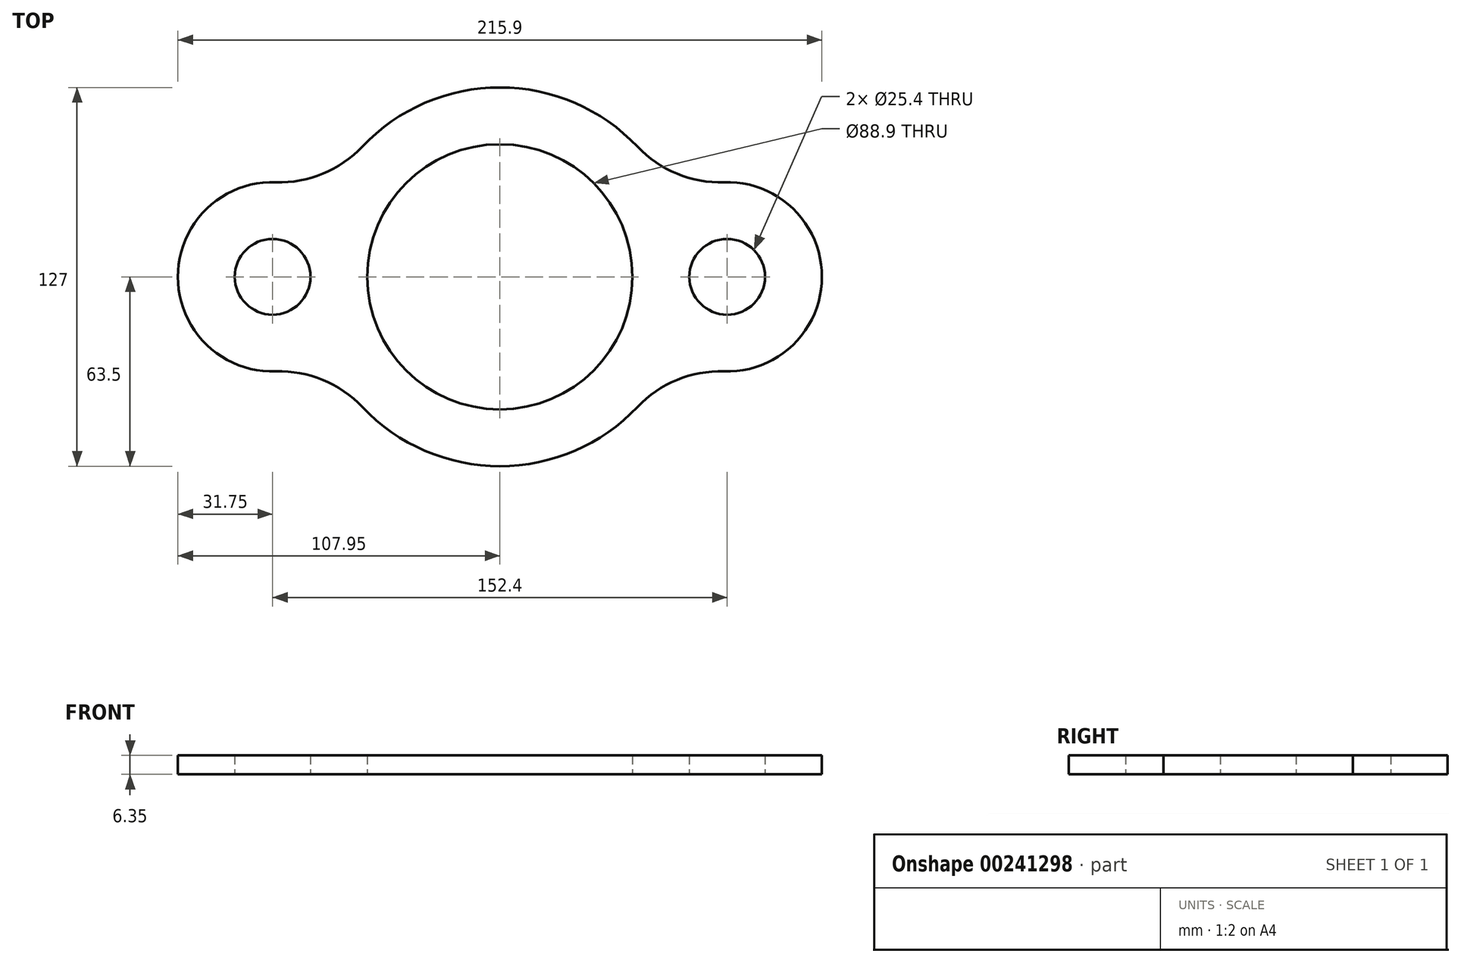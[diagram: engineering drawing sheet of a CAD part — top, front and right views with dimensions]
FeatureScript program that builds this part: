
annotation { "Feature Type Name" : "Feature", "Feature Type Description" : "" }
export const myFeature = defineFeature(function(context is Context, id is Id, definition is map)
    precondition{}
    {
        {
            var Q0;
            Q0=qCreatedBy(makeId("Top.planeOp"),FACE);
            var sketch = newSketch(context, id + "F0", { "sketchPlane" : qUnion([Q0])});
            skCircle(sketch, "E0", {"center": v(0, 0) * mm, "radius": 44.45 * mm});
            skArc(sketch, "E1", {"start": v(-46.14, -43.63) * mm, "mid": v(0, -63.5) * mm, "end": v(46.14, -43.63) * mm});
            skCircle(sketch, "E2", {"center": v(-76.2, 0) * mm, "radius": 12.7 * mm});
            skCircle(sketch, "E3", {"center": v(76.2, 0) * mm, "radius": 12.7 * mm});
            skLineSegment(sketch, "E4", {"start": v(0, 0) * mm, "end": v(-76.2, 0) * mm, "construction": true});
            skArc(sketch, "E5", {"start": v(-75.12, 31.73) * mm, "mid": v(-107.95, 0) * mm, "end": v(-75.12, -31.73) * mm});
            skArc(sketch, "E6", {"start": v(75.12, -31.73) * mm, "mid": v(107.95, 0) * mm, "end": v(75.12, 31.73) * mm});
            skLineSegment(sketch, "E7", {"start": v(0, 0) * mm, "end": v(76.2, 0) * mm, "construction": true});
            skArc(sketch, "E8.trimOffspring", {"start": v(46.14, 43.63) * mm, "mid": v(0, 63.5) * mm, "end": v(-46.14, 43.63) * mm});
            skPoint(sketch, "E9.visualSharp", {"position": v(-57.94, 25.98) * mm});
            skArc(sketch, "E9.filletArc", {"start": v(-75.12, 31.73) * mm, "mid": v(-59.35, 34.56) * mm, "end": v(-46.14, 43.63) * mm});
            skPoint(sketch, "E10.visualSharp", {"position": v(57.94, 25.98) * mm});
            skArc(sketch, "E10.filletArc", {"start": v(46.14, 43.63) * mm, "mid": v(59.35, 34.56) * mm, "end": v(75.12, 31.73) * mm});
            skPoint(sketch, "E11.visualSharp", {"position": v(57.94, -25.98) * mm});
            skArc(sketch, "E11.filletArc", {"start": v(75.12, -31.73) * mm, "mid": v(59.35, -34.56) * mm, "end": v(46.14, -43.63) * mm});
            skPoint(sketch, "E12.visualSharp", {"position": v(-57.94, -25.98) * mm});
            skArc(sketch, "E12.filletArc", {"start": v(-46.14, -43.63) * mm, "mid": v(-59.35, -34.56) * mm, "end": v(-75.12, -31.73) * mm});
            skSolve(sketch);
        }
        {
            var Q0;
            Q0=makeQuery(id+"F0.imprint","IMPRINT",FACE,{"disambiguationData":[TD([[makeQuery(id+"F0.imprint","IMPRINT",EDGE,{"derivedFrom":sQuery(id+"F0.wireOp",EDGE,"E1")}),1.0]])]});
            extrude(context, id + "F1", {"entities" : qUnion([Q0]), "depth" : 6.35 * mm});
        }
    });
